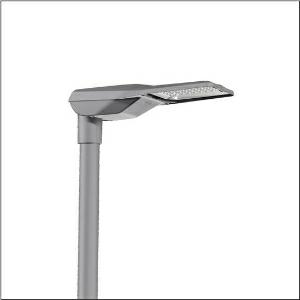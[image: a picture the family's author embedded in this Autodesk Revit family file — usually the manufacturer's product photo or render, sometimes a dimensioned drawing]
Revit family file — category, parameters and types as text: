
# Revit family: streetlight_sl_21_iq_mini___st1_5a_5xe2p31g08gb_08f7
name_source: partatom
category: Lighting Fixtures
units: mm (PartAtom-declared; Revit-internal decimal feet)

## family parameters
Cut with Voids When Loaded = No
Host = Face
Light Source = No
Part Type = Normal
Room Calculation Point = No
Round Connector Dimension = Use Diameter
Shared = No

## types (1)
- --- (1 x LED, 5580 lm, 37.1 W, 3000K)
    Apparent Load = 37 VA
    CIE Flux Codes = 22 53 95 100 100
    Color Rendering = 70
    Color Temperature = 3000K
    Default Elevation = 1800 mm
    Description = Streetlight SL 21 iQ mini, mast luminaire, primary light control with lens, of PMMA, primary optical cover: cover, of toughened safety glass, transparent, light distribution: ST1.5a, light emission: direct distribution, primary light characteristic: asymmetric, installation type: post-top, side-entry, LED, High Power LED, rated luminous flux: 5.580lm, luminous efficacy: 150lm/W, light colour: 730, colour temperature: 3000K, control gear: iQ Street-Remote, control: Street-Remote, Auto-Match, Temp-Guard, Lumen-Switch, Night-Set, Smart-Wire, Light-Fading, Desk-Remote (wireless, voltage-free reading and setting of iQ features in the workshop via application-optimized NFC function/RFID function), optimised constant luminous flux control (CLO 2.0), pre-setting: linear dimming characteristic, mains connection: 220..240V, AC, 50/60Hz, start of lifetime: 37W, end of service life: 39W, reduction: 18W, luminaire housing, of diecast aluminium, powder-coated, SITECO metallic grey (DB 702S), corrosivity category C5 high according to DIN EN ISO 12944, please order mast flange separately, inclination adjustable: 0°, 5°, 10°, 15°, sealing non-destructively replaceable, multi-level sealing system, length: 628mm, width: 235mm, height: 110mm, mast flange for spigot size: 42mm (side-entry): 5XC10008XM4, 60/48mm (side-entry/post-top): 5XC10108XM2, 76/60mm (side-entry/post-top): 5XC10108XM1, mounting height: 4..8m, protection rating (complete): IP66, insulation class (complete): insulation class II (safety insulation), certification: CE, ENEC, ENEC+, VDE, impact resistance: IK10, permissible operating ambient temperature for outdoor applications: -40..+50°C, standard-compliant lighting for roads and squares, packaging unit: 1 piece

Light Distribution: ST1.5a
    Height = 110 mm
    Lamp = 1 x LED
    Lamp Light Flux = 5580 lm
    Lamp Power = 37.1 W
    Lamp count = 1
    Length = 625 mm
    Luminous efficacy = 150 lm/W
    Manufacturer = Siteco
    ModVariant = No
    Model = 5XE2P31G08GB
    Number of Poles = 1
    OnlyDefault = Yes
    Power Factor = 1
    Product Name = Streetlight SL 21 iQ mini | ST1.5a
    Product group = mast luminaire | pylon top
    ProductGroupID = 6100
    Protection Class = Protection class II
    Protection Degree = IP 66
    RLX_Detail_Level = 1
    RLX_Emergency_Light_Flux = 0 lm
    RLX_Emergency_Type = 0
    RLX_Emergency_Type_DB = No
    RlxData = <blob elided: 29869 chars, md5=6e1180b0>
    Socket = socket
    Standby Power = 0 W
    System Light Flux = 5580 lm
    System Power = 37 W
    Type Comments = factory setting: luminous flux: 100 % | dim-lin: 254 | 385 mA
    Type Image = l_1003519.jpg
    URL = http://relux.com
    VarID = @adj_175313
    Voltage = 0 V
    Weight = 0.00 kg
    Width = 234 mm

## geometry (parser evidence)
native form markers: Blend x4, Sweep x11
no freeform markers — native parametric forms only
